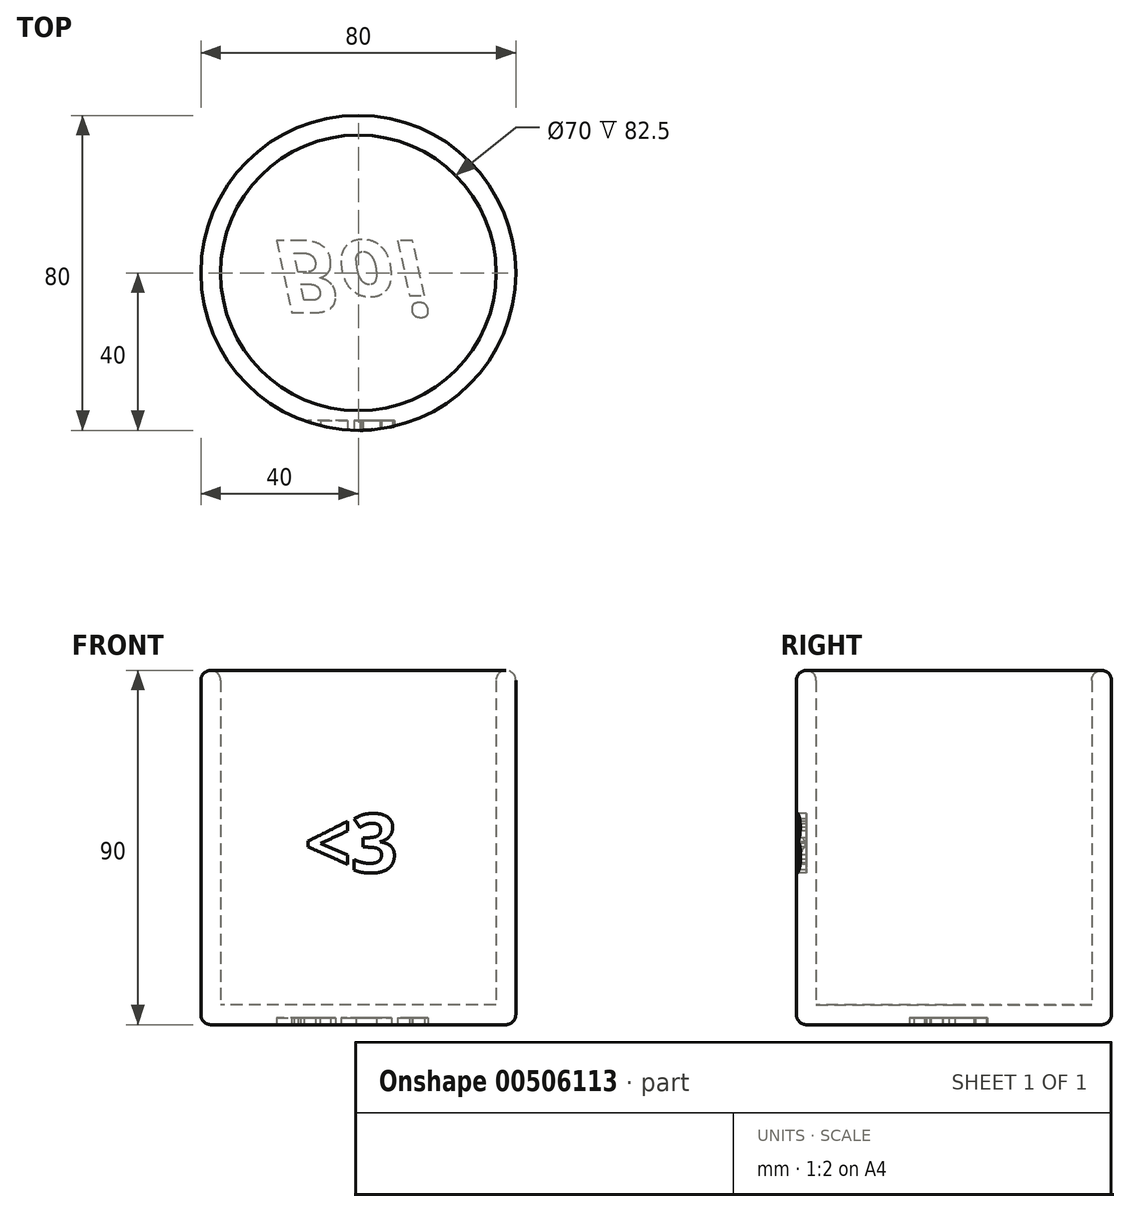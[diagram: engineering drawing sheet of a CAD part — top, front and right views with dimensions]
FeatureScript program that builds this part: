
annotation { "Feature Type Name" : "Feature", "Feature Type Description" : "" }
export const myFeature = defineFeature(function(context is Context, id is Id, definition is map)
    precondition{}
    {
        {
            var Q0;
            Q0=qCreatedBy(makeId("Top.planeOp"),FACE);
            var sketch = newSketch(context, id + "F0", { "sketchPlane" : qUnion([Q0])});
            skCircle(sketch, "E0", {"center": v(0, 0) * mm, "radius": 40 * mm});
            skSolve(sketch);
        }
        {
            var Q0;
            Q0=makeQuery(id+"F0.imprint","IMPRINT",FACE,{"disambiguationData":[TD([[makeQuery(id+"F0.imprint","IMPRINT",EDGE,{"derivedFrom":sQuery(id+"F0.wireOp",EDGE,"E0")}),1.0]])]});
            extrude(context, id + "F1", {"entities" : qUnion([Q0]), "depth" : 90 * mm});
        }
        {
            var Q0;
            Q0=makeQuery(id+"F1.opExtrude","CAP_FACE",FACE,{"disambiguationData":[OSD([sQuery(id+"F0.wireOp",EDGE,"E0")])],"isStart":false});
            shell(context, id + "F2", {"entities" : qUnion([Q0]), "thickness" : 5 * mm});
        }
        {
            var Q0;
            Q0=qCreatedBy(makeId("Right.planeOp"),FACE);
            cPlane(context, id + "F3", {"entities" : qUnion([Q0]), "cplaneType" : CPlaneType.OFFSET, "offset" : 36.8 * mm, "width" : 150 * mm, "height" : 150 * mm});
        }
        {
            var Q0;
            Q0=qCreatedBy(id+"F3.planeOp",FACE);
            var sketch = newSketch(context, id + "F4", { "sketchPlane" : qUnion([Q0])});
            skCircle(sketch, "E1", {"center": v(0, 72) * mm, "radius": 5 * mm});
            skSolve(sketch);
        }
        {
            var Q0;
            Q0=qCreatedBy(id+"F3.planeOp",FACE);
            var sketch = newSketch(context, id + "F5", { "sketchPlane" : qUnion([Q0])});
            skLineSegment(sketch, "E2", {"start": v(-8.7, 44.66) * mm, "end": v(15.41, 44.66) * mm});
            skSolve(sketch);
        }
        {
            var Q0;
            Q0=sQuery(id+"F4.wireOp",EDGE,"E1");
            var Q1;
            Q1=sQuery(id+"F5.wireOp",EDGE,"E2");
            revolve(context, id + "F6", {"bodyType" : ToolBodyType.SURFACE, "surfaceEntities" : qUnion([Q0]), "axis" : qUnion([Q1]), "revolveType" : RevolveType.ONE_DIRECTION, "angle" : 180 * degree});
        }
        {
            var Q0;
            Q0=makeQuery(id+"F1.opExtrude","CAP_EDGE",EDGE,{"disambiguationData":[OSD([sQuery(id+"F0.wireOp",EDGE,"E0")])],"isStart":false});
            var Q1;
            {var subQ0=sQuery(id+"F0.wireOp",EDGE,"E0");Q1=makeQuery(id+"F2.opShell","OFFSET_EDGE",EDGE,{"disambiguationData":[OSD([subQ0]),TDD([makeQuery(id+"F1.opExtrude","CAP_EDGE",EDGE,{"disambiguationData":[OSD([subQ0])],"isStart":false})])]});}
            var Q2;
            Q2=makeQuery(id+"F1.opExtrude","CAP_FACE",FACE,{"disambiguationData":[OSD([sQuery(id+"F0.wireOp",EDGE,"E0")])],"isStart":true});
            fillet(context, id + "F7", {"entities" : qUnion([Q0, Q1, Q2]), "radius" : 2.5 * mm, "tangentPropagation" : true, "allowEdgeOverflow" : false});
        }
        {
            var Q0;
            Q0=makeQuery(id+"F1.opExtrude","CAP_FACE",FACE,{"disambiguationData":[OSD([sQuery(id+"F0.wireOp",EDGE,"E0")])],"isStart":true});
            var sketch = newSketch(context, id + "F8", { "sketchPlane" : qUnion([Q0])});
            skText(sketch, "E3", { "text": "Boi", "fontName": "OpenSans-BoldItalic.ttf"});
            const initialGuessF8  = {"E3": [-0.02147, -0.00825, 1, 0, 0.01853]};
            skSetInitialGuess(sketch, initialGuessF8);
            skSolve(sketch);
        }
        {
            var Q0;
            Q0 = qSketchRegion(id + "F8", true);
            extrude(context, id + "F9", {"entities" : qUnion([Q0]), "operationType" : NewBodyOperationType.REMOVE, "oppositeDirection" : true, "depth" : 1.75 * mm});
        }
        {
            var Q0;
            Q0=qCreatedBy(makeId("Front.planeOp"),FACE);
            cPlane(context, id + "F10", {"entities" : qUnion([Q0]), "cplaneType" : CPlaneType.OFFSET, "offset" : 40 * mm, "width" : 150 * mm, "height" : 150 * mm});
        }
        {
            var Q0;
            Q0=qCreatedBy(id+"F10.planeOp",FACE);
            var sketch = newSketch(context, id + "F11", { "sketchPlane" : qUnion([Q0])});
            skText(sketch, "E4", { "text": "<3", "fontName": "OpenSans-Bold.ttf"});
            const initialGuessF11  = {"E4": [-0.01367, 0.0387, 1, 0, 0.01491]};
            skSetInitialGuess(sketch, initialGuessF11);
            skSolve(sketch);
        }
        {
            var Q0;
            Q0 = qSketchRegion(id + "F11", true);
            extrude(context, id + "F12", {"entities" : qUnion([Q0]), "operationType" : NewBodyOperationType.REMOVE, "oppositeDirection" : true, "depth" : 2.5 * mm});
        }
    });
